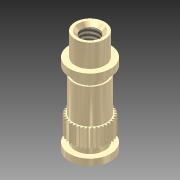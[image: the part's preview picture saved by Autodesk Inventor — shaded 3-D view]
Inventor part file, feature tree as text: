
AUTODESK INVENTOR PART (.ipt)
format: ipt  version: 2011 (Build 150239000, 239)  size: 241,664 bytes
history: native  units: in
note: dims shown in document units (in); Inventor stores cm internally (conversion verified against a paired STEP export)
features: other x1, imported_body x1, thread x1
ambient origin geometry x8: Origin, YZ Plane, XZ Plane, XY Plane, X Axis, Y Axis, Z Axis, Center Point
feature tree (3):
  parser-record x1  (decoder bookkeeping rows leaked as tree rows — omitted from the tree; the rows remain in map.json)
  imported_body  "Base1"
  thread  "Thread1"  [1 undecoded]
note: 1 required parameter value undecoded (feature->parameter linkage not recoverable at this tier; creation-order binding heuristic only, values carry confidence <= 0.55)
